# Revit family: Control_Panels-Lutron-QS_Wireless_Smart
name_source: partatom
category: Lighting Devices
revit_build: Autodesk Revit 2017 (Build: 20160720_1515(x64)
units: mm (PartAtom-declared; Revit-internal decimal feet)

## family parameters
Cut with Voids When Loaded = No
Host = Face
Maintain Annotation Orientation = Yes
OmniClass Number = 23.80.30.11.17
OmniClass Title = Distribution Boards and Control Panels
Part Type = Normal
Room Calculation Point = No
Round Connector Dimension = Use Radius
Shared = No

## types (1)
- QSPSY-10PNL
    Assembly Code = D5020
    Cost = 0 $
    Cover Depth = 0' - 0"
    Cover Material = Steel - Lutron - Black
    Current = 10 A
    Default Elevation = 6' - 6"
    Description = Sivoia® QS Wireless Smart Panel
    Frequency = 60 Hz
    Instruction Sheet Link = http://www.lutron.com
    Load Classification = Other
    Manufacturer = Lutron Electronics Co., Inc
    Manufacturer Fax Number = 610-282-1243
    Maximum Operating Temperature = 104 °F
    Minimum Operating Temperature = 32 °F
    Model = QSPSY-10PNL
    Output Current = 0 A
    Output Voltage = 35.00 V
    Overall Depth = 0' - 4"
    Overall Height = 1' - 6"
    Overall Width = 0' - 11"
    Panel Depth = 0' - 4"
    Panel Height = 1' - 5 1/2"
    Panel Material = Steel - Lutron - Chrome Plated
    Panel Thickness = 0' - 0"
    Panel Width = 0' - 10 1/2"
    Performance URL = http://www.lutron.com
    Product Documentation Link = http://www.lutron.com
    Product Name = Sivoia QS Wireless Smart Panel
    Product Page URL = http://www.lutron.com
    Series = Sivoia® QS
    Surface Mounted = Yes
    URL = http://www.lutron.com
    Unit Weight = 15.00 lb
    Version = 2017 - v1.0b
    Video Link = https://www.youtube.com
    Voltage = 0.00 V
    Voltage Comment = 120 to 240
    Warranty URL = http://www.lutron.com

## geometry (parser evidence)
native form markers: Sweep x3
no freeform markers — native parametric forms only
